# Revit family: BDG_BossDesign_Stng_Kruze
name_source: partatom
category: Furniture
revit_build: Autodesk Revit 2015 (Build: 20140903_1530(x64)
units: mm (PartAtom-declared; Revit-internal decimal feet)

## types (20) — shared parameters
Assembly Code = E2020200
AssetType = Movable
BIMObjectName = BDG_BossDesign_Seating_Kruze
Category = Pr_40_50_12 : Chairs, seats and benches
CodePerformance = BS EN13761: 2002
DurationUnit = year
ExpectedLife = 5
IfcExportAs = IfcFurnishingElementType
IfcExportType = CHAIR
Keynote = Pr_40_50_12
ManufacturerName = Boss Design
ManufacturerURL = www.bossdesign.com
NBSDescription = Seating
NBSReference = 45-35-72/352
Name = Seating_Kruze_BossDesign
NominalHeight = 850 mm  [stored 2.78871 ft]
ProductInformation = www.bossdesign.com/product-list/kruze/
Revision = 1
Shape = Rectangular
SustainabilityPerformance = 85.85% Recyclable
URL = www.bossdesign.com
Uniclass2015Description = Chairs, seats and benches
Uniclass2015Reference = Pr_40_50_12
Uniclass2015Version = Products v1.9
Version = 1
WarrantyDescription = Structural Warranty Excludes Foams and Fabrics
WarrantyDurationLabor = 5
WarrantyDurationParts = 5
WarrantyDurationUnit = year

## per-type parameters (varying)
| type | Features | Finish | Has4StarBase | Has4StarBaseCastor | Is4Leg | Is5StarBase | IsSledBase | IsUpholsteredShell | IsWoodFrame | IsWoodShell | Material | Model | ModelNumber | NominalLength | NominalWidth | ShellMaterial | Size |
| Fully Upholstered 4 Leg | 4 Leg | Upholstered | No | No | Yes | No | No | Yes | No | No | Fabric | KRU/1 | KRU/1 | 640 mm  [stored 2.09974 ft] | 610 mm  [stored 2.00131 ft] | BDG_Generic_Wood_Walnut_BlackAmerican | 640 x 610 x 850mm |
| Fully Upholstered 4 Star Base | 4 Star Base | Upholstered | Yes | No | No | No | No | Yes | No | No | Fabric | KRU/2 | KRU/2 | 610 mm  [stored 2.00131 ft] | 610 mm  [stored 2.00131 ft] | BDG_Generic_Wood_Walnut_BlackAmerican | 610 x 610 x 850mm |
| Fully Upholstered 4 Star Base with Castors | 4 Star Base with Castors | Upholstered | No | Yes | No | No | No | Yes | No | No | Fabric | KRU/2/P4 | KRU/2/P4 | 610 mm  [stored 2.00131 ft] | 610 mm  [stored 2.00131 ft] | BDG_Generic_Wood_Walnut_BlackAmerican | 610 x 610 x 850mm |
| Fully Upholstered 5 Star Base with Castors | 5 Star Base with Castors | Upholstered | No | No | No | Yes | No | Yes | No | No | Fabric | KRU/2/P5 | KRU/2/P5 | 690 mm  [stored 2.26378 ft] | 460 mm  [stored 1.50919 ft] | BDG_Generic_Wood_Walnut_BlackAmerican | 690 x 460 x 850mm |
| Oak Outershell 4 Star Base with Castors | 4 Star Base with Castors | Oak Outershell | No | Yes | No | No | No | No | No | Yes | Fabric/Wood | KRU/4/O/P4 | KRU/4/O/P4 | 610 mm  [stored 2.00131 ft] | 610 mm  [stored 2.00131 ft] | BDG_Generic_Wood_Oak | 610 x 610 x 850mm |
| Oak Outershell 4 Star Base | 4 Star Base | Oak Outershell | Yes | No | No | No | No | No | No | Yes | Fabric/Wood | KRU/4/O | KRU/4/O | 610 mm  [stored 2.00131 ft] | 610 mm  [stored 2.00131 ft] | BDG_Generic_Wood_Oak | 610 x 610 x 850mm |
| Oak Outershell 5 Star Base with Castors | 5 Star Base with Castors | Oak Outershell | No | No | No | Yes | No | No | No | Yes | Fabric/Wood | KRU/4/O/P5 | KRU/4/O/P5 | 690 mm  [stored 2.26378 ft] | 460 mm  [stored 1.50919 ft] | BDG_Generic_Wood_Oak | 690 x 460 x 850mm |
| Walnut Outershell 4 Star Base | 4 Star Base | Walnut Outershell | Yes | No | No | No | No | No | No | Yes | Fabric/Wood | KRU/4/W | KRU/4/W | 610 mm  [stored 2.00131 ft] | 610 mm  [stored 2.00131 ft] | BDG_Generic_Wood_Walnut_BlackAmerican | 610 x 610 x 850mm |
| Walnut Outershell 4 Star Base with Castors | 4 Star Base with Castors | Walnut Outershell | No | Yes | No | No | No | No | No | Yes | Fabric/Wood | KRU/4/W/P4 | KRU/4/W/P4 | 610 mm  [stored 2.00131 ft] | 610 mm  [stored 2.00131 ft] | BDG_Generic_Wood_Walnut_BlackAmerican | 610 x 610 x 850mm |
| Walnut Outershell 5 Star Base with Castors | 5 Star Base with Castors | Walnut Outershell | No | No | No | Yes | No | No | No | Yes | Fabric/Wood | KRU/4/W/P5 | KRU/4/W/P5 | 690 mm  [stored 2.26378 ft] | 460 mm  [stored 1.50919 ft] | BDG_Generic_Wood_Walnut_BlackAmerican | 690 x 460 x 850mm |
| Oak Outershell 4 Leg | 4 Leg | Oak Outershell | No | No | Yes | No | No | No | No | Yes | Fabric/Wood | KRU/3/O | KRU/3/O | 640 mm  [stored 2.09974 ft] | 610 mm  [stored 2.00131 ft] | BDG_Generic_Wood_Oak | 640 x 610 x 850mm |
| Walnut Outershell 4 Leg | 4 Leg | Walnut Outershell | No | No | Yes | No | No | No | No | Yes | Fabric/Wood | KRU/3/W | KRU/3/W | 640 mm  [stored 2.09974 ft] | 610 mm  [stored 2.00131 ft] | BDG_Generic_Wood_Walnut_BlackAmerican | 640 x 610 x 850mm |
| Fully Upholstered Sled Base | Sled Base | Upholstered | No | No | No | No | Yes | Yes | No | No | Fabric | KRU/13 | KRU/13 | 630 mm  [stored 2.06693 ft] | 605 mm  [stored 1.98491 ft] | BDG_Generic_Wood_Walnut_BlackAmerican | 630 x 605 x 850mm |
| Oak Outershell Sled Base | Sled Base | Oak Outershell | No | No | No | No | Yes | No | No | Yes | Fabric/Wood | KRU/14/O | KRU/14/O | 630 mm  [stored 2.06693 ft] | 605 mm  [stored 1.98491 ft] | BDG_Generic_Wood_Oak | 630 x 605 x 850mm |
| Walnut Outershell Sled Base | Sled Base | Walnut Outershell | No | No | No | No | Yes | No | No | Yes | Fabric/Wood | KRU/14/W | KRU/14/W | 630 mm  [stored 2.06693 ft] | 605 mm  [stored 1.98491 ft] | BDG_Generic_Wood_Walnut_BlackAmerican | 630 x 605 x 850mm |
| Fully Upholstered Oak Base | Oak Base | Upholstered | No | No | No | No | No | Yes | Yes | No | Fabric/Wood | KRU/2/OF | KRU/2/OF | 645 mm  [stored 2.11614 ft] | 605 mm  [stored 1.98491 ft] | BDG_Generic_Wood_Oak | 645 x 605 x 850mm |
| Fully Upholstered Walnut Base | Walnut Base | Upholstered | No | No | No | No | No | Yes | Yes | No | Fabric/Wood | KRU/2/WF | KRU/2/WF | 645 mm  [stored 2.11614 ft] | 605 mm  [stored 1.98491 ft] | BDG_Generic_Wood_Walnut_BlackAmerican | 645 x 605 x 850mm |
| Oak Outershell Oak Base | Oak Base | Oak Outershell | No | No | No | No | No | No | Yes | Yes | Fabric/Wood | KRU/4/O/OF | KRU/4/O/OF | 645 mm  [stored 2.11614 ft] | 605 mm  [stored 1.98491 ft] | BDG_Generic_Wood_Oak | 645 x 605 x 850mm |
| Walnut Outershell Walnut Base | Walnut Base | Walnut Outershell | No | No | No | No | No | No | Yes | Yes | Fabric/Wood | KRU/4/W/WF | KRU/4/W/WF | 645 mm  [stored 2.11614 ft] | 605 mm  [stored 1.98491 ft] | BDG_Generic_Wood_Walnut_BlackAmerican | 645 x 605 x 850mm |
| Fully Upholstered Painted Sled Base | Painted Sled Base | Upholstered | No | No | No | No | Yes | Yes | No | No | Fabric | KRU/13/PF | KRU/13/PF | 630 mm  [stored 2.06693 ft] | 605 mm  [stored 1.98491 ft] | BDG_Generic_Wood_Walnut_BlackAmerican | 630 x 605 x 850mm |

note: column(s) folded — value = type name in every type: Description, ModelReference

note: [stored X ft] marks values corroborated as IEEE doubles in the binary element streams (Revit-internal decimal feet)

## geometry (parser evidence)
native form markers: Blend x152, Sweep x1
no freeform markers — native parametric forms only
